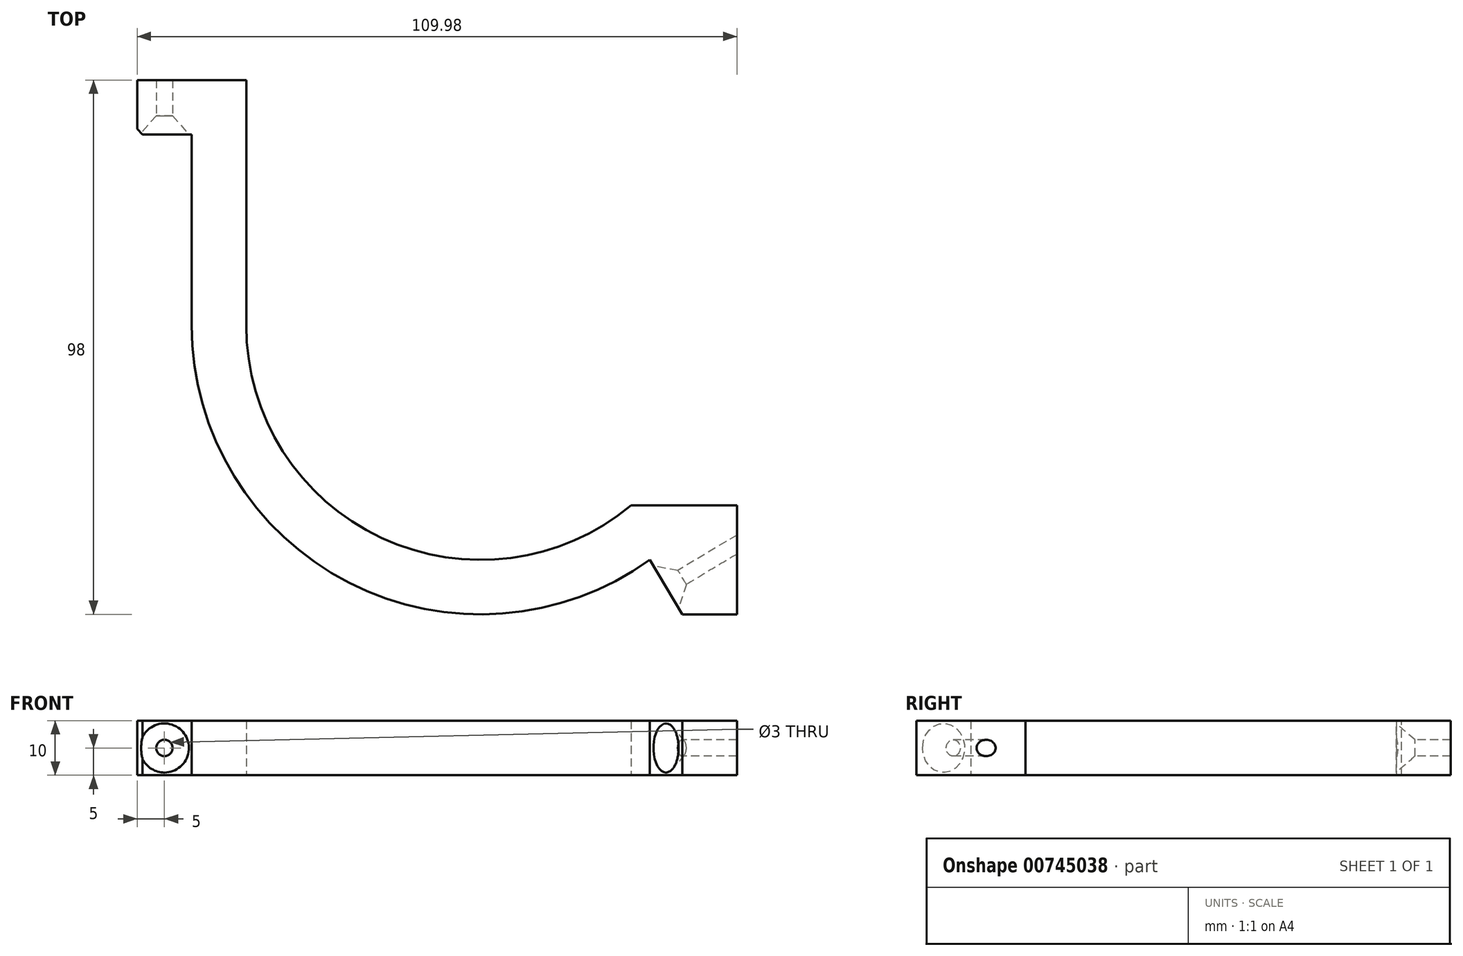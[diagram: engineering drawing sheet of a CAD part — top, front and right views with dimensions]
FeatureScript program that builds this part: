
annotation { "Feature Type Name" : "Feature", "Feature Type Description" : "" }
export const myFeature = defineFeature(function(context is Context, id is Id, definition is map)
    precondition{}
    {
        {
            var Q0;
            Q0=qCreatedBy(makeId("Top.planeOp"),FACE);
            var sketch = newSketch(context, id + "F0", { "sketchPlane" : qUnion([Q0])});
            skArc(sketch, "E0", {"start": v(-43, 0) * mm, "mid": v(-18.21, -38.95) * mm, "end": v(27.57, -33) * mm});
            skArc(sketch, "E1", {"start": v(-53, 0) * mm, "mid": v(-24.15, -47.18) * mm, "end": v(30.98, -43) * mm});
            skLineSegment(sketch, "E2", {"start": v(-53, 0) * mm, "end": v(-53, 45) * mm});
            skLineSegment(sketch, "E3", {"start": v(-43, 0) * mm, "end": v(-43, 45) * mm});
            skLineSegment(sketch, "E4", {"start": v(-43, 45) * mm, "end": v(-53, 45) * mm});
            skLineSegment(sketch, "E5.bottom", {"start": v(-53, 45) * mm, "end": v(-63, 45) * mm});
            skLineSegment(sketch, "E5.top", {"start": v(-53, 35) * mm, "end": v(-63, 35) * mm});
            skLineSegment(sketch, "E5.left", {"start": v(-53, 45) * mm, "end": v(-53, 35) * mm});
            skLineSegment(sketch, "E5.right", {"start": v(-63, 45) * mm, "end": v(-63, 35) * mm});
            skLineSegment(sketch, "E6", {"start": v(46.98, -33) * mm, "end": v(27.57, -33) * mm});
            skPoint(sketch, "E7.orphan", {"position": v(0, -43) * mm});
            skLineSegment(sketch, "E8", {"start": v(46.98, -33) * mm, "end": v(46.98, -43) * mm});
            skLineSegment(sketch, "E9", {"start": v(46.98, -43) * mm, "end": v(46.98, -53) * mm});
            skLineSegment(sketch, "E10", {"start": v(46.98, -53) * mm, "end": v(36.98, -53) * mm});
            skLineSegment(sketch, "E11", {"start": v(36.98, -53) * mm, "end": v(30.98, -43) * mm});
            skSolve(sketch);
        }
        {
            var Q0;
            Q0=makeQuery(id+"F0.imprint","IMPRINT",FACE,{"disambiguationData":[TD([[makeQuery(id+"F0.imprint","IMPRINT",EDGE,{"derivedFrom":sQuery(id+"F0.wireOp",EDGE,"E0")}),-1.0]])]});
            var Q1;
            {var subQ0=sQuery(id+"F0.wireOp",EDGE,"E5.bottom");Q1=makeQuery(id+"F0.imprint","IMPRINT",FACE,{"disambiguationData":[TD([[makeQuery(id+"F0.imprint","IMPRINT",EDGE,{"derivedFrom":subQ0}),1.0]])]});}
            extrude(context, id + "F1", {"entities" : qUnion([Q0, Q1]), "depth" : 10 * mm, "offsetDistance" : 25 * mm});
        }
        {
            var Q0;
            Q0=makeQuery(id+"F1.opExtrude","SWEPT_FACE",FACE,{"disambiguationData":[OSD([sQuery(id+"F0.wireOp",EDGE,"E5.top")])]});
            var sketch = newSketch(context, id + "F2", { "sketchPlane" : qUnion([Q0])});
            skPoint(sketch, "E12", {"position": v(-58, 5) * mm});
            skPoint(sketch, "E12.positionSnap0", {"position": v(-63, 5) * mm});
            skPoint(sketch, "E12.positionSnap1", {"position": v(-58, 0) * mm});
            skSolve(sketch);
        }
        {
            var Q0;
            Q0=makeQuery(id+"F1.opExtrude","SWEPT_FACE",FACE,{"disambiguationData":[OSD([sQuery(id+"F0.wireOp",EDGE,"E11")])]});
            var sketch = newSketch(context, id + "F3", { "sketchPlane" : qUnion([Q0])});
            skPoint(sketch, "E13", {"position": v(58.64, 5) * mm});
            skPoint(sketch, "E13.positionSnap0", {"position": v(64.48, 5) * mm});
            skPoint(sketch, "E13.positionSnap1", {"position": v(58.64, 10) * mm});
            skSolve(sketch);
        }
        {
            var Q0;
            Q0=sQuery(id+"F3.wireOp",VERTEX,"E13");
            var Q1;
            Q1=sQuery(id+"F2.wireOp",VERTEX,"E12");
            var Q2;
            Q2=makeQuery(id+"F1.opExtrude","SWEPT_BODY",BODY,{"disambiguationData":[OSD([sQuery(id+"F0.wireOp",EDGE,"E0"),sQuery(id+"F0.wireOp",EDGE,"E1"),sQuery(id+"F0.wireOp",EDGE,"E2"),sQuery(id+"F0.wireOp",EDGE,"E3"),sQuery(id+"F0.wireOp",EDGE,"E4"),sQuery(id+"F0.wireOp",EDGE,"E5.bottom"),sQuery(id+"F0.wireOp",EDGE,"E5.top"),sQuery(id+"F0.wireOp",EDGE,"E5.right"),sQuery(id+"F0.wireOp",EDGE,"E6"),sQuery(id+"F0.wireOp",EDGE,"E8"),sQuery(id+"F0.wireOp",EDGE,"E9"),sQuery(id+"F0.wireOp",EDGE,"E10"),sQuery(id+"F0.wireOp",EDGE,"E11")])]});
            hole(context, id + "F4", {"style" : HoleStyle.C_SINK, "endStyle" : HoleEndStyle.THROUGH, "holeDiameter" : 3 * mm, "cSinkDiameter" : 9 * mm, "cSinkAngle" : 82 * degree, "majorDiameter" : 5 * mm, "isTappedThrough" : true, "tappedDepth" : 6 * mm, "tapClearance" : 3, "locations" : qUnion([Q0, Q1]), "scope" : qUnion([Q2])});
        }
        {
            var Q0;
            Q0=makeQuery(id+"F1.opExtrude","SWEPT_EDGE",EDGE,{"disambiguationData":[OSD([sQuery(id+"F0.wireOp",EDGE,"E5.top"),sQuery(id+"F0.wireOp",EDGE,"E5.right")])]});
            chamfer(context, id + "F5", {"entities" : qUnion([Q0]), "width" : 1 * mm, "tangentPropagation" : true});
        }
    });
